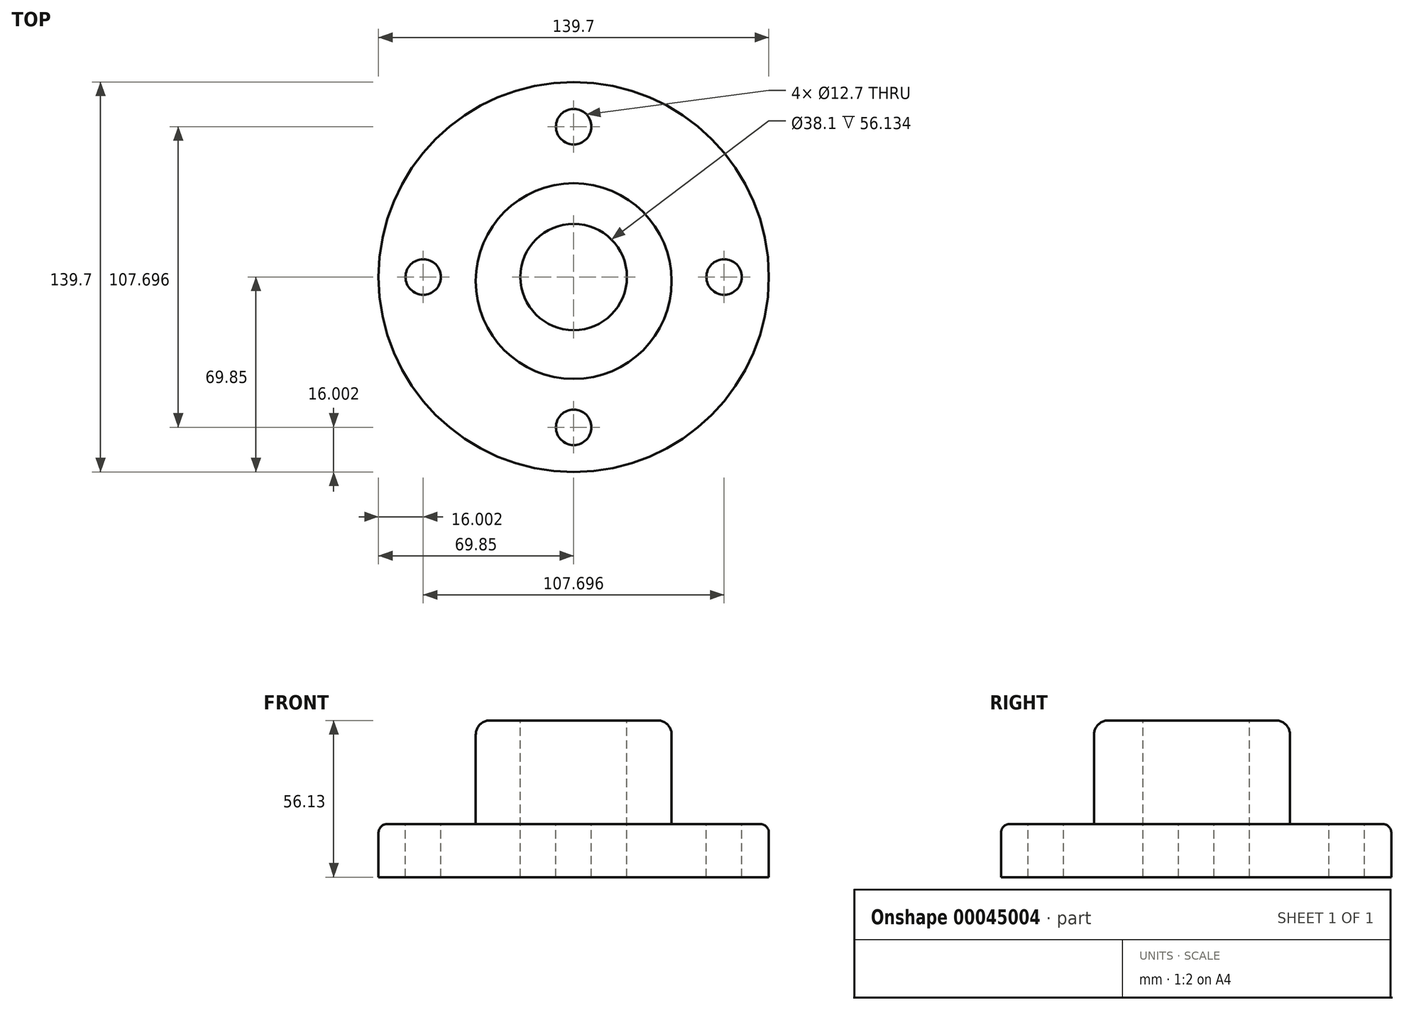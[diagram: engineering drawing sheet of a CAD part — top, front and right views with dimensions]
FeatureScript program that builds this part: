
annotation { "Feature Type Name" : "Feature", "Feature Type Description" : "" }
export const myFeature = defineFeature(function(context is Context, id is Id, definition is map)
    precondition{}
    {
        {
            var Q0;
            Q0=qCreatedBy(makeId("Top.planeOp"),FACE);
            var sketch = newSketch(context, id + "F0", { "sketchPlane" : qUnion([Q0])});
            skCircle(sketch, "E0", {"center": v(0, 0) * mm, "radius": 69.85 * mm});
            skSolve(sketch);
        }
        {
            var Q0;
            Q0=makeQuery(id+"F0.imprint","IMPRINT",FACE,{"disambiguationData":[TD([[makeQuery(id+"F0.imprint","IMPRINT",EDGE,{"derivedFrom":sQuery(id+"F0.wireOp",EDGE,"E0")}),1.0]])]});
            extrude(context, id + "F1", {"entities" : qUnion([Q0]), "depth" : 19.05 * mm});
        }
        {
            var Q0;
            Q0=makeQuery(id+"F1.opExtrude","CAP_FACE",FACE,{"disambiguationData":[OSD([sQuery(id+"F0.wireOp",EDGE,"E0")])],"isStart":false});
            var sketch = newSketch(context, id + "F2", { "sketchPlane" : qUnion([Q0])});
            skCircle(sketch, "E1", {"center": v(0, -1.48) * mm, "radius": 35.05 * mm});
            skSolve(sketch);
        }
        {
            var Q0;
            Q0=makeQuery(id+"F2.imprint","IMPRINT",FACE,{"disambiguationData":[TD([[makeQuery(id+"F2.imprint","IMPRINT",EDGE,{"derivedFrom":sQuery(id+"F2.wireOp",EDGE,"E1")}),1.0]])]});
            extrude(context, id + "F3", {"entities" : qUnion([Q0]), "operationType" : NewBodyOperationType.ADD, "depth" : 37.08 * mm});
        }
        {
            var Q0;
            Q0=makeQuery(id+"F3.opExtrude","CAP_FACE",FACE,{"disambiguationData":[OSD([sQuery(id+"F2.wireOp",EDGE,"E1")])],"isStart":false});
            var sketch = newSketch(context, id + "F4", { "sketchPlane" : qUnion([Q0])});
            skCircle(sketch, "E2", {"center": v(0, 0) * mm, "radius": 19.05 * mm});
            skSolve(sketch);
        }
        {
            var Q0;
            Q0=makeQuery(id+"F4.imprint","IMPRINT",FACE,{"disambiguationData":[TD([[makeQuery(id+"F4.imprint","IMPRINT",EDGE,{"derivedFrom":sQuery(id+"F4.wireOp",EDGE,"E2")}),1.0]])]});
            extrude(context, id + "F5", {"entities" : qUnion([Q0]), "operationType" : NewBodyOperationType.REMOVE, "endBound" : BoundingType.THROUGH_ALL, "oppositeDirection" : true, "depth" : 25.4 * mm});
        }
        {
            var Q0;
            Q0=makeQuery(id+"F1.opExtrude","CAP_FACE",FACE,{"disambiguationData":[OSD([sQuery(id+"F0.wireOp",EDGE,"E0")])],"isStart":false});
            var sketch = newSketch(context, id + "F6", { "sketchPlane" : qUnion([Q0])});
            skCircle(sketch, "E3", {"center": v(0, 0) * mm, "radius": 53.85 * mm, "construction": true});
            skPoint(sketch, "E4", {"position": v(0, 53.85) * mm});
            skPoint(sketch, "E5", {"position": v(53.85, 0) * mm});
            skPoint(sketch, "E6", {"position": v(0, -53.85) * mm});
            skPoint(sketch, "E7", {"position": v(-53.85, 0) * mm});
            skSolve(sketch);
        }
        {
            var Q0;
            Q0=sQuery(id+"F6.wireOp",VERTEX,"E4");
            var Q1;
            Q1=sQuery(id+"F6.wireOp",VERTEX,"E5");
            var Q2;
            Q2=sQuery(id+"F6.wireOp",VERTEX,"E6");
            var Q3;
            Q3=sQuery(id+"F6.wireOp",VERTEX,"E7");
            var Q4;
            Q4=makeQuery(id+"F1.opExtrude","SWEPT_BODY",BODY,{"disambiguationData":[OSD([sQuery(id+"F0.wireOp",EDGE,"E0")])]});
            hole(context, id + "F7", {"style" : HoleStyle.SIMPLE, "holeDiameter" : 12.7 * mm, "endStyle" : HoleEndStyle.THROUGH, "locations" : qUnion([Q0, Q1, Q2, Q3]), "scope" : qUnion([Q4])});
        }
        {
            var Q0;
            Q0=makeQuery(id+"F1.opExtrude","CAP_EDGE",EDGE,{"disambiguationData":[OSD([sQuery(id+"F0.wireOp",EDGE,"E0")])],"isStart":false});
            var Q1;
            Q1=makeQuery(id+"F3.opExtrude","CAP_EDGE",EDGE,{"disambiguationData":[OSD([sQuery(id+"F2.wireOp",EDGE,"E1")])],"isStart":true});
            fillet(context, id + "F8", {"entities" : qUnion([Q0, Q1]), "radius" : 3.17 * mm, "tangentPropagation" : true, "allowEdgeOverflow" : false});
        }
        {
            var Q0;
            Q0=makeQuery(id+"F3.opExtrude","CAP_EDGE",EDGE,{"disambiguationData":[OSD([sQuery(id+"F2.wireOp",EDGE,"E1")])],"isStart":false});
            fillet(context, id + "F9", {"entities" : qUnion([Q0]), "radius" : 5.08 * mm, "tangentPropagation" : true, "allowEdgeOverflow" : false});
        }
    });
